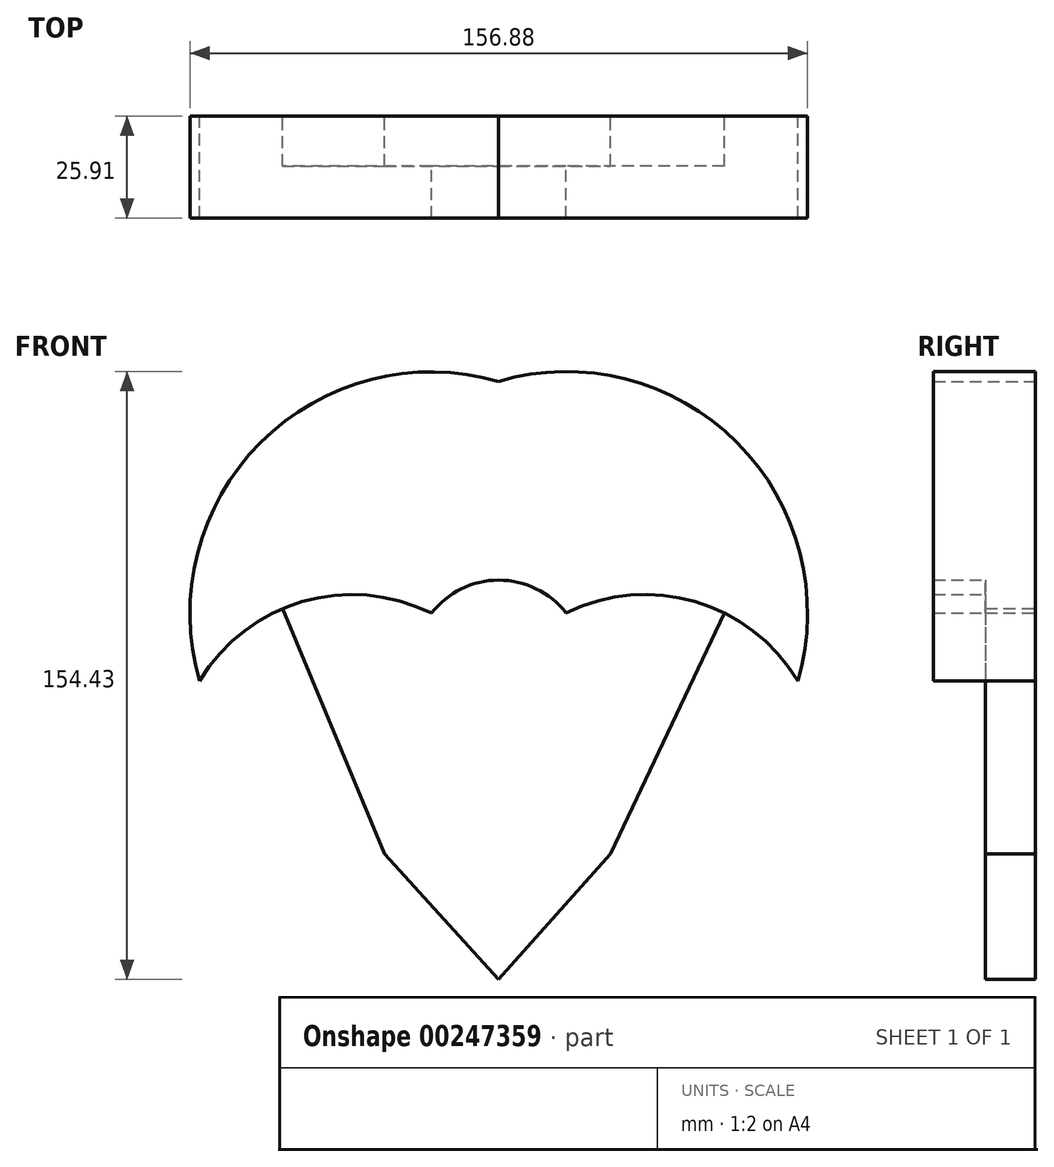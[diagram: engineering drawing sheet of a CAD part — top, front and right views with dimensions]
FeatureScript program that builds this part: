
annotation { "Feature Type Name" : "Feature", "Feature Type Description" : "" }
export const myFeature = defineFeature(function(context is Context, id is Id, definition is map)
    precondition{}
    {
        {
            var Q0;
            Q0=qCreatedBy(makeId("Front.planeOp"),FACE);
            var sketch = newSketch(context, id + "F0", { "sketchPlane" : qUnion([Q0])});
            skArc(sketch, "E0", {"start": v(0, 76.08) * mm, "mid": v(-60.43, 60.47) * mm, "end": v(-75.88, 0) * mm});
            skArc(sketch, "E1", {"start": v(76.08, 0) * mm, "mid": v(60.59, 60.59) * mm, "end": v(0, 76.08) * mm});
            skArc(sketch, "E2", {"start": v(-17.01, 17.16) * mm, "mid": v(-49.8, 20.09) * mm, "end": v(-75.88, 0) * mm});
            skArc(sketch, "E3", {"start": v(76.08, 0) * mm, "mid": v(50, 20.08) * mm, "end": v(17.23, 17.23) * mm});
            skArc(sketch, "E4", {"start": v(17.23, 17.23) * mm, "mid": v(0.1, 25.56) * mm, "end": v(-17.01, 17.16) * mm});
            skLineSegment(sketch, "E5", {"start": v(-54.81, 18.3) * mm, "end": v(-28.9, -44.03) * mm});
            skLineSegment(sketch, "E6", {"start": v(-28.9, -44.03) * mm, "end": v(0.13, 3.86) * mm});
            skLineSegment(sketch, "E7", {"start": v(57.44, 17.17) * mm, "end": v(28.5, -44.03) * mm});
            skLineSegment(sketch, "E8", {"start": v(28.5, -44.03) * mm, "end": v(0.13, 3.86) * mm});
            skLineSegment(sketch, "E9", {"start": v(-28.9, -44.03) * mm, "end": v(0, -75.88) * mm});
            skLineSegment(sketch, "E10", {"start": v(0, -75.88) * mm, "end": v(28.5, -44.03) * mm});
            skSolve(sketch);
        }
        {
            var Q0;
            {var subQ1=sQuery(id+"F0.wireOp",EDGE,"E0");Q0=makeQuery(id+"F0.imprint","IMPRINT",FACE,{"disambiguationData":[TD([[makeQuery(id+"F0.imprint","IMPRINT",EDGE,{"derivedFrom":subQ1}),1.0]])]});}
            extrude(context, id + "F1", {"entities" : qUnion([Q0]), "depth" : 25.9 * mm});
        }
        {
            var Q0;
            Q0 = qSketchRegion(id + "F0", true);
            extrude(context, id + "F2", {"entities" : qUnion([Q0]), "operationType" : NewBodyOperationType.ADD, "depth" : 12.7 * mm});
        }
    });
